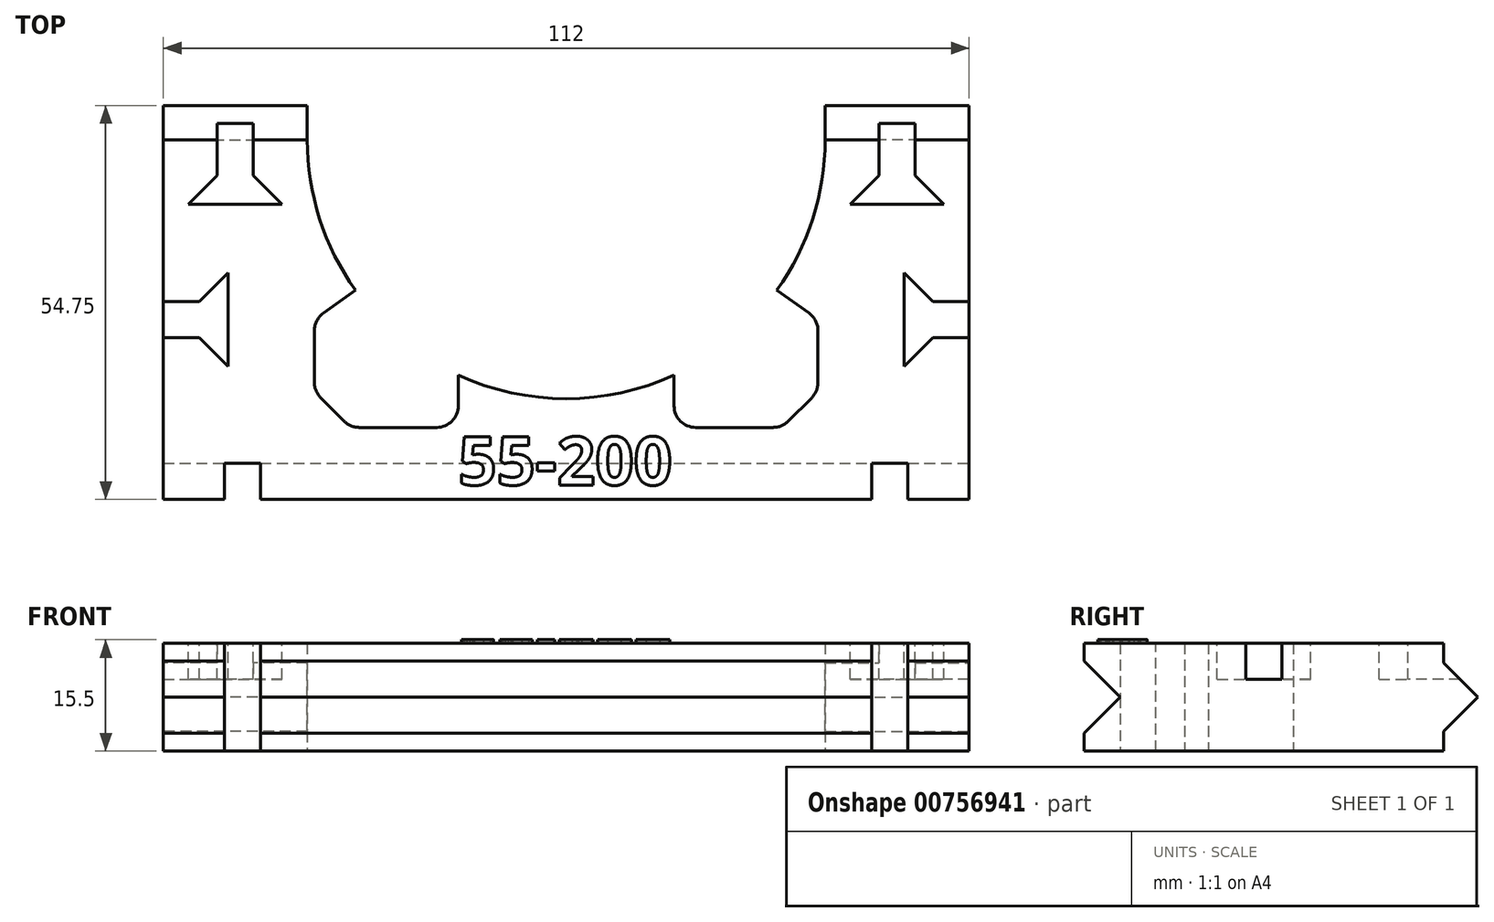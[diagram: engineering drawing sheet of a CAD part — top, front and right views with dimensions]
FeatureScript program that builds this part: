
annotation { "Feature Type Name" : "Feature", "Feature Type Description" : "" }
export const myFeature = defineFeature(function(context is Context, id is Id, definition is map)
    precondition{}
    {
        {
            var Q0;
            Q0=qCreatedBy(makeId("Top.planeOp"),FACE);
            var sketch = newSketch(context, id + "F0", { "sketchPlane" : qUnion([Q0])});
            skLineSegment(sketch, "E0", {"start": v(-56, 0) * mm, "end": v(56, 0) * mm});
            skLineSegment(sketch, "E1", {"start": v(56, 0) * mm, "end": v(56, 50) * mm});
            skLineSegment(sketch, "E2", {"start": v(56, 50) * mm, "end": v(36, 50) * mm});
            skLineSegment(sketch, "E3", {"start": v(-56, 0) * mm, "end": v(-56, 50) * mm});
            skLineSegment(sketch, "E4", {"start": v(-56, 50) * mm, "end": v(-36, 50) * mm});
            skCircle(sketch, "E5", {"center": v(0, 50) * mm, "radius": 36 * mm, "construction": true});
            skPoint(sketch, "E5.centerSnap0", {"position": v(-46, 50) * mm});
            skArc(sketch, "E6", {"start": v(-36, 50) * mm, "mid": v(0, 14) * mm, "end": v(36, 50) * mm});
            skLineSegment(sketch, "E7", {"start": v(-15, 17.27) * mm, "end": v(-15, 10) * mm});
            skLineSegment(sketch, "E8", {"start": v(-15, 10) * mm, "end": v(-35, 10) * mm});
            skLineSegment(sketch, "E9", {"start": v(-35, 10) * mm, "end": v(-35, 25) * mm});
            skLineSegment(sketch, "E10", {"start": v(-35, 25) * mm, "end": v(-29.3, 29.08) * mm});
            skArc(sketch, "E11", {"start": v(-15, 17.27) * mm, "mid": v(-22.92, 22.24) * mm, "end": v(-29.3, 29.08) * mm});
            skLineSegment(sketch, "E12.MirrorCS", {"start": v(35, 25) * mm, "end": v(29.3, 29.08) * mm});
            skLineSegment(sketch, "E13.MirrorCS", {"start": v(35, 10) * mm, "end": v(35, 25) * mm});
            skLineSegment(sketch, "E14.MirrorCS", {"start": v(15, 10) * mm, "end": v(35, 10) * mm});
            skLineSegment(sketch, "E15.MirrorCS", {"start": v(15, 17.27) * mm, "end": v(15, 10) * mm});
            skArc(sketch, "E16.MirrorCS", {"start": v(15, 17.27) * mm, "mid": v(22.92, 22.24) * mm, "end": v(29.3, 29.08) * mm});
            skSolve(sketch);
        }
        {
            var Q0;
            Q0=makeQuery(id+"F0.imprint","IMPRINT",FACE,{"disambiguationData":[TD([[makeQuery(id+"F0.imprint","IMPRINT",EDGE,{"derivedFrom":sQuery(id+"F0.wireOp",EDGE,"E0")}),1.0]])]});
            extrude(context, id + "F1", {"entities" : qUnion([Q0]), "depth" : 15 * mm, "offsetDistance" : 25 * mm});
        }
        {
            var Q0;
            Q0=makeQuery(id+"F1.opExtrude","SWEPT_EDGE",EDGE,{"disambiguationData":[OSD([sQuery(id+"F0.wireOp",EDGE,"E8"),sQuery(id+"F0.wireOp",EDGE,"E9")])]});
            var Q1;
            Q1=makeQuery(id+"F1.opExtrude","SWEPT_EDGE",EDGE,{"disambiguationData":[OSD([sQuery(id+"F0.wireOp",EDGE,"E13.MirrorCS"),sQuery(id+"F0.wireOp",EDGE,"E14.MirrorCS")])]});
            chamfer(context, id + "F2", {"entities" : qUnion([Q0, Q1]), "width" : 5 * mm, "tangentPropagation" : true});
        }
        {
            var Q0;
            Q0=makeQuery(id+"F1.opExtrude","SWEPT_EDGE",EDGE,{"disambiguationData":[OSD([sQuery(id+"F0.wireOp",EDGE,"E7"),sQuery(id+"F0.wireOp",EDGE,"E8")])]});
            var Q1;
            {var subQ0=sQuery(id+"F0.wireOp",EDGE,"E8");Q1=makeQuery(id+"F2.opChamfer","BLEND_EDGE",EDGE,{"blendedFrom":[makeQuery(id+"F1.opExtrude","SWEPT_EDGE",EDGE,{"disambiguationData":[OSD([subQ0,sQuery(id+"F0.wireOp",EDGE,"E9")])]}),makeQuery(id+"F1.opExtrude","SWEPT_FACE",FACE,{"disambiguationData":[OSD([subQ0])]})],"blendedInto":[makeQuery(id+"F1.opExtrude","SWEPT_FACE",FACE,{"disambiguationData":[OSD([subQ0])]})]});}
            var Q2;
            {var subQ0=sQuery(id+"F0.wireOp",EDGE,"E9");Q2=makeQuery(id+"F2.opChamfer","BLEND_EDGE",EDGE,{"blendedFrom":[makeQuery(id+"F1.opExtrude","SWEPT_EDGE",EDGE,{"disambiguationData":[OSD([sQuery(id+"F0.wireOp",EDGE,"E8"),subQ0])]}),makeQuery(id+"F1.opExtrude","SWEPT_FACE",FACE,{"disambiguationData":[OSD([subQ0])]})],"blendedInto":[makeQuery(id+"F1.opExtrude","SWEPT_FACE",FACE,{"disambiguationData":[OSD([subQ0])]})]});}
            var Q3;
            Q3=makeQuery(id+"F1.opExtrude","SWEPT_EDGE",EDGE,{"disambiguationData":[OSD([sQuery(id+"F0.wireOp",EDGE,"E9"),sQuery(id+"F0.wireOp",EDGE,"E10")])]});
            var Q4;
            Q4=makeQuery(id+"F1.opExtrude","SWEPT_EDGE",EDGE,{"disambiguationData":[OSD([sQuery(id+"F0.wireOp",EDGE,"E14.MirrorCS"),sQuery(id+"F0.wireOp",EDGE,"E15.MirrorCS")])]});
            var Q5;
            {var subQ0=sQuery(id+"F0.wireOp",EDGE,"E14.MirrorCS");Q5=makeQuery(id+"F2.opChamfer","BLEND_EDGE",EDGE,{"blendedFrom":[makeQuery(id+"F1.opExtrude","SWEPT_EDGE",EDGE,{"disambiguationData":[OSD([sQuery(id+"F0.wireOp",EDGE,"E13.MirrorCS"),subQ0])]}),makeQuery(id+"F1.opExtrude","SWEPT_FACE",FACE,{"disambiguationData":[OSD([subQ0])]})],"blendedInto":[makeQuery(id+"F1.opExtrude","SWEPT_FACE",FACE,{"disambiguationData":[OSD([subQ0])]})]});}
            var Q6;
            {var subQ0=sQuery(id+"F0.wireOp",EDGE,"E13.MirrorCS");Q6=makeQuery(id+"F2.opChamfer","BLEND_EDGE",EDGE,{"blendedFrom":[makeQuery(id+"F1.opExtrude","SWEPT_EDGE",EDGE,{"disambiguationData":[OSD([subQ0,sQuery(id+"F0.wireOp",EDGE,"E14.MirrorCS")])]}),makeQuery(id+"F1.opExtrude","SWEPT_FACE",FACE,{"disambiguationData":[OSD([subQ0])]})],"blendedInto":[makeQuery(id+"F1.opExtrude","SWEPT_FACE",FACE,{"disambiguationData":[OSD([subQ0])]})]});}
            var Q7;
            Q7=makeQuery(id+"F1.opExtrude","SWEPT_EDGE",EDGE,{"disambiguationData":[OSD([sQuery(id+"F0.wireOp",EDGE,"E12.MirrorCS"),sQuery(id+"F0.wireOp",EDGE,"E13.MirrorCS")])]});
            fillet(context, id + "F3", {"entities" : qUnion([Q0, Q1, Q2, Q3, Q4, Q5, Q6, Q7]), "radius" : 3 * mm, "tangentPropagation" : true, "allowEdgeOverflow" : false});
        }
        {
            var Q0;
            Q0=makeQuery(id+"F1.opExtrude","SWEPT_FACE",FACE,{"disambiguationData":[OSD([sQuery(id+"F0.wireOp",EDGE,"E3")])]});
            var sketch = newSketch(context, id + "F4", { "sketchPlane" : qUnion([Q0])});
            skLineSegment(sketch, "E17", {"start": v(-50, 2.75) * mm, "end": v(-54.75, 7.5) * mm});
            skPoint(sketch, "E17.endSnap0", {"position": v(-50, 7.5) * mm});
            skLineSegment(sketch, "E18", {"start": v(-54.75, 7.5) * mm, "end": v(-50, 12.25) * mm});
            skLineSegment(sketch, "E19", {"start": v(-50, 12.25) * mm, "end": v(-50, 2.75) * mm});
            skSolve(sketch);
        }
        {
            var Q0;
            Q0=makeQuery(id+"F4.imprint","IMPRINT",FACE,{"disambiguationData":[TD([[makeQuery(id+"F4.imprint","IMPRINT",EDGE,{"derivedFrom":sQuery(id+"F4.wireOp",EDGE,"E17")}),-1.0]])]});
            extrude(context, id + "F5", {"entities" : qUnion([Q0]), "operationType" : NewBodyOperationType.ADD, "oppositeDirection" : true, "depth" : 20 * mm, "offsetDistance" : 25 * mm});
        }
        {
            var Q0;
            Q0=makeQuery(id+"F1.opExtrude","SWEPT_FACE",FACE,{"disambiguationData":[OSD([sQuery(id+"F0.wireOp",EDGE,"E1")])]});
            var sketch = newSketch(context, id + "F6", { "sketchPlane" : qUnion([Q0])});
            skLineSegment(sketch, "E20.0", {"start": v(54.75, 7.5) * mm, "end": v(50, 12.25) * mm});
            skLineSegment(sketch, "E21.0", {"start": v(50, 2.75) * mm, "end": v(54.75, 7.5) * mm});
            skLineSegment(sketch, "E22.0.1", {"start": v(50, 12.25) * mm, "end": v(50, 2.75) * mm});
            skSolve(sketch);
        }
        {
            var Q0;
            Q0=makeQuery(id+"F6.imprint","IMPRINT",FACE,{"disambiguationData":[TD([[makeQuery(id+"F6.imprint","IMPRINT",EDGE,{"derivedFrom":sQuery(id+"F6.wireOp",EDGE,"E20.0")}),1.0]])]});
            extrude(context, id + "F7", {"entities" : qUnion([Q0]), "operationType" : NewBodyOperationType.ADD, "oppositeDirection" : true, "depth" : 20 * mm, "offsetDistance" : 25 * mm});
        }
        {
            var Q0;
            Q0=makeQuery(id+"F1.opExtrude","CAP_FACE",FACE,{"disambiguationData":[OSD([sQuery(id+"F0.wireOp",EDGE,"E0"),sQuery(id+"F0.wireOp",EDGE,"E1"),sQuery(id+"F0.wireOp",EDGE,"E2"),sQuery(id+"F0.wireOp",EDGE,"E3"),sQuery(id+"F0.wireOp",EDGE,"E4"),sQuery(id+"F0.wireOp",EDGE,"E6"),sQuery(id+"F0.wireOp",EDGE,"E7"),sQuery(id+"F0.wireOp",EDGE,"E8"),sQuery(id+"F0.wireOp",EDGE,"E9"),sQuery(id+"F0.wireOp",EDGE,"E10"),sQuery(id+"F0.wireOp",EDGE,"E12.MirrorCS"),sQuery(id+"F0.wireOp",EDGE,"E13.MirrorCS"),sQuery(id+"F0.wireOp",EDGE,"E14.MirrorCS"),sQuery(id+"F0.wireOp",EDGE,"E15.MirrorCS")])],"isStart":false});
            var sketch = newSketch(context, id + "F8", { "sketchPlane" : qUnion([Q0])});
            skLineSegment(sketch, "E23", {"start": v(-56, 22.5) * mm, "end": v(-51, 22.5) * mm});
            skLineSegment(sketch, "E24", {"start": v(-51, 22.5) * mm, "end": v(-47, 18.5) * mm});
            skLineSegment(sketch, "E25", {"start": v(-47, 18.5) * mm, "end": v(-47, 31.5) * mm});
            skLineSegment(sketch, "E26", {"start": v(-47, 31.5) * mm, "end": v(-51, 27.5) * mm});
            skLineSegment(sketch, "E27", {"start": v(-51, 27.5) * mm, "end": v(-56, 27.5) * mm});
            skLineSegment(sketch, "E28", {"start": v(-56, 27.5) * mm, "end": v(-56, 22.5) * mm});
            skLineSegment(sketch, "E29.MirrorCS", {"start": v(47, 18.5) * mm, "end": v(47, 31.5) * mm});
            skLineSegment(sketch, "E30.MirrorCS", {"start": v(47, 31.5) * mm, "end": v(51, 27.5) * mm});
            skLineSegment(sketch, "E31.MirrorCS", {"start": v(51, 22.5) * mm, "end": v(47, 18.5) * mm});
            skLineSegment(sketch, "E32.MirrorCS", {"start": v(56, 22.5) * mm, "end": v(51, 22.5) * mm});
            skLineSegment(sketch, "E33.MirrorCS", {"start": v(56, 27.5) * mm, "end": v(56, 22.5) * mm});
            skLineSegment(sketch, "E34.MirrorCS", {"start": v(51, 27.5) * mm, "end": v(56, 27.5) * mm});
            skSolve(sketch);
        }
        {
            var Q0;
            Q0 = qSketchRegion(id + "F8", true);
            extrude(context, id + "F9", {"entities" : qUnion([Q0]), "operationType" : NewBodyOperationType.REMOVE, "oppositeDirection" : true, "depth" : 5 * mm, "offsetDistance" : 25 * mm});
        }
        {
            var Q0;
            Q0=makeQuery(id+"F7.boolean.opBoolean","MERGE",FACE,{"derivedFrom":[makeQuery(id+"F1.opExtrude","SWEPT_FACE",FACE,{"disambiguationData":[OSD([sQuery(id+"F0.wireOp",EDGE,"E1")])]}),makeQuery(id+"F7.opExtrude","CAP_FACE",FACE,{"disambiguationData":[OSD([sQuery(id+"F6.wireOp",EDGE,"E20.0"),sQuery(id+"F6.wireOp",EDGE,"E22.0.1"),sQuery(id+"F6.wireOp",EDGE,"E21.0")])],"isStart":true})]});
            var sketch = newSketch(context, id + "F10", { "sketchPlane" : qUnion([Q0])});
            skLineSegment(sketch, "E35", {"start": v(0, 12.5) * mm, "end": v(0, 2.5) * mm});
            skLineSegment(sketch, "E36", {"start": v(0, 2.5) * mm, "end": v(5, 7.5) * mm});
            skLineSegment(sketch, "E37", {"start": v(5, 7.5) * mm, "end": v(0, 12.5) * mm});
            skSolve(sketch);
        }
        {
            var Q0;
            Q0 = qSketchRegion(id + "F10", true);
            extrude(context, id + "F11", {"entities" : qUnion([Q0]), "operationType" : NewBodyOperationType.REMOVE, "endBound" : BoundingType.THROUGH_ALL, "oppositeDirection" : true, "depth" : 25 * mm, "offsetDistance" : 25 * mm});
        }
        {
            var Q0;
            Q0=makeQuery(id+"F1.opExtrude","CAP_FACE",FACE,{"disambiguationData":[OSD([sQuery(id+"F0.wireOp",EDGE,"E0"),sQuery(id+"F0.wireOp",EDGE,"E1"),sQuery(id+"F0.wireOp",EDGE,"E2"),sQuery(id+"F0.wireOp",EDGE,"E3"),sQuery(id+"F0.wireOp",EDGE,"E4"),sQuery(id+"F0.wireOp",EDGE,"E6"),sQuery(id+"F0.wireOp",EDGE,"E7"),sQuery(id+"F0.wireOp",EDGE,"E8"),sQuery(id+"F0.wireOp",EDGE,"E9"),sQuery(id+"F0.wireOp",EDGE,"E10"),sQuery(id+"F0.wireOp",EDGE,"E12.MirrorCS"),sQuery(id+"F0.wireOp",EDGE,"E13.MirrorCS"),sQuery(id+"F0.wireOp",EDGE,"E14.MirrorCS"),sQuery(id+"F0.wireOp",EDGE,"E15.MirrorCS")])],"isStart":true});
            var sketch = newSketch(context, id + "F12", { "sketchPlane" : qUnion([Q0])});
            skLineSegment(sketch, "E38", {"start": v(47.5, 0) * mm, "end": v(47.5, -5) * mm});
            skLineSegment(sketch, "E39", {"start": v(47.5, -5) * mm, "end": v(42.5, -5) * mm});
            skLineSegment(sketch, "E40", {"start": v(42.5, -5) * mm, "end": v(42.5, 0) * mm});
            skLineSegment(sketch, "E41", {"start": v(42.5, 0) * mm, "end": v(47.5, 0) * mm});
            skLineSegment(sketch, "E42.MirrorCS", {"start": v(-47.5, 0) * mm, "end": v(-47.5, -5) * mm});
            skLineSegment(sketch, "E43.MirrorCS", {"start": v(-47.5, -5) * mm, "end": v(-42.5, -5) * mm});
            skLineSegment(sketch, "E44.MirrorCS", {"start": v(-42.5, -5) * mm, "end": v(-42.5, 0) * mm});
            skLineSegment(sketch, "E45.MirrorCS", {"start": v(-42.5, 0) * mm, "end": v(-47.5, 0) * mm});
            skSolve(sketch);
        }
        {
            var Q0;
            Q0 = qSketchRegion(id + "F12", true);
            extrude(context, id + "F13", {"entities" : qUnion([Q0]), "operationType" : NewBodyOperationType.REMOVE, "oppositeDirection" : true, "depth" : 25 * mm, "offsetDistance" : 25 * mm});
        }
        {
            var Q0;
            Q0=makeQuery(id+"F1.opExtrude","CAP_FACE",FACE,{"disambiguationData":[OSD([sQuery(id+"F0.wireOp",EDGE,"E0"),sQuery(id+"F0.wireOp",EDGE,"E1"),sQuery(id+"F0.wireOp",EDGE,"E2"),sQuery(id+"F0.wireOp",EDGE,"E3"),sQuery(id+"F0.wireOp",EDGE,"E4"),sQuery(id+"F0.wireOp",EDGE,"E6"),sQuery(id+"F0.wireOp",EDGE,"E7"),sQuery(id+"F0.wireOp",EDGE,"E8"),sQuery(id+"F0.wireOp",EDGE,"E9"),sQuery(id+"F0.wireOp",EDGE,"E10"),sQuery(id+"F0.wireOp",EDGE,"E12.MirrorCS"),sQuery(id+"F0.wireOp",EDGE,"E13.MirrorCS"),sQuery(id+"F0.wireOp",EDGE,"E14.MirrorCS"),sQuery(id+"F0.wireOp",EDGE,"E15.MirrorCS")])],"isStart":false});
            var sketch = newSketch(context, id + "F14", { "sketchPlane" : qUnion([Q0])});
            skLineSegment(sketch, "E46", {"start": v(-52.5, 41) * mm, "end": v(-39.5, 41) * mm});
            skLineSegment(sketch, "E47", {"start": v(-39.5, 41) * mm, "end": v(-43.5, 45) * mm});
            skLineSegment(sketch, "E48", {"start": v(-43.5, 45) * mm, "end": v(-43.5, 50) * mm});
            skLineSegment(sketch, "E49", {"start": v(-43.5, 50) * mm, "end": v(-48.5, 50) * mm, "construction": true});
            skLineSegment(sketch, "E50", {"start": v(-48.5, 50) * mm, "end": v(-48.5, 45) * mm});
            skLineSegment(sketch, "E51", {"start": v(-48.5, 45) * mm, "end": v(-52.5, 41) * mm});
            skLineSegment(sketch, "E52", {"start": v(-48.5, 50) * mm, "end": v(-48.5, 55.42) * mm});
            skLineSegment(sketch, "E53", {"start": v(-48.5, 55.42) * mm, "end": v(-43.5, 55.42) * mm});
            skLineSegment(sketch, "E54", {"start": v(-43.5, 55.42) * mm, "end": v(-43.5, 50) * mm});
            skPoint(sketch, "E55.endSnap0", {"position": v(-46, 55.42) * mm});
            skLineSegment(sketch, "E56.MirrorCS", {"start": v(48.5, 55.42) * mm, "end": v(43.5, 55.42) * mm});
            skLineSegment(sketch, "E57.MirrorCS", {"start": v(43.5, 50) * mm, "end": v(48.5, 50) * mm, "construction": true});
            skLineSegment(sketch, "E58.MirrorCS", {"start": v(52.5, 41) * mm, "end": v(39.5, 41) * mm});
            skPoint(sketch, "E59.MirrorP", {"position": v(46, 55.42) * mm});
            skLineSegment(sketch, "E60.MirrorCS", {"start": v(39.5, 41) * mm, "end": v(43.5, 45) * mm});
            skLineSegment(sketch, "E61.MirrorCS", {"start": v(48.5, 50) * mm, "end": v(48.5, 45) * mm});
            skLineSegment(sketch, "E62.MirrorCS", {"start": v(48.5, 50) * mm, "end": v(48.5, 55.42) * mm});
            skLineSegment(sketch, "E63.MirrorCS", {"start": v(43.5, 55.42) * mm, "end": v(43.5, 50) * mm});
            skLineSegment(sketch, "E64.MirrorCS", {"start": v(43.5, 45) * mm, "end": v(43.5, 50) * mm});
            skLineSegment(sketch, "E65.MirrorCS", {"start": v(48.5, 45) * mm, "end": v(52.5, 41) * mm});
            skSolve(sketch);
        }
        {
            var Q0;
            Q0 = qSketchRegion(id + "F14", true);
            extrude(context, id + "F15", {"entities" : qUnion([Q0]), "operationType" : NewBodyOperationType.REMOVE, "oppositeDirection" : true, "depth" : 5 * mm, "offsetDistance" : 25 * mm});
        }
        {
            var Q0;
            Q0=makeQuery(id+"F1.opExtrude","CAP_FACE",FACE,{"disambiguationData":[OSD([sQuery(id+"F0.wireOp",EDGE,"E0"),sQuery(id+"F0.wireOp",EDGE,"E1"),sQuery(id+"F0.wireOp",EDGE,"E2"),sQuery(id+"F0.wireOp",EDGE,"E3"),sQuery(id+"F0.wireOp",EDGE,"E4"),sQuery(id+"F0.wireOp",EDGE,"E6"),sQuery(id+"F0.wireOp",EDGE,"E7"),sQuery(id+"F0.wireOp",EDGE,"E8"),sQuery(id+"F0.wireOp",EDGE,"E9"),sQuery(id+"F0.wireOp",EDGE,"E10"),sQuery(id+"F0.wireOp",EDGE,"E12.MirrorCS"),sQuery(id+"F0.wireOp",EDGE,"E13.MirrorCS"),sQuery(id+"F0.wireOp",EDGE,"E14.MirrorCS"),sQuery(id+"F0.wireOp",EDGE,"E15.MirrorCS")])],"isStart":false});
            var sketch = newSketch(context, id + "F16", { "sketchPlane" : qUnion([Q0])});
            skText(sketch, "E66", { "text": "55-200", "fontName": "OpenSans-Bold.ttf"});
            const initialGuessF16  = {"E66": [-0.015, 0.002, 1, 0, 0.00674]};
            skSetInitialGuess(sketch, initialGuessF16);
            skSolve(sketch);
        }
        {
            var Q0;
            Q0 = qSketchRegion(id + "F16", true);
            extrude(context, id + "F17", {"entities" : qUnion([Q0]), "operationType" : NewBodyOperationType.ADD, "depth" : 0.5 * mm, "offsetDistance" : 25 * mm});
        }
    });
